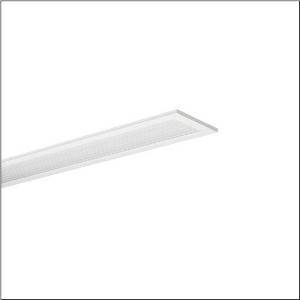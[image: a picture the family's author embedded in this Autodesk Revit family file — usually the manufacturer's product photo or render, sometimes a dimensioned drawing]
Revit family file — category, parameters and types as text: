
# Revit family: apollon_21_linear_51mq15wm2414
name_source: partatom
category: Lighting Fixtures
units: mm (PartAtom-declared; Revit-internal decimal feet)

## family parameters
Cut with Voids When Loaded = No
Host = Face
Light Source = No
Part Type = Normal
Room Calculation Point = No
Round Connector Dimension = Use Diameter
Shared = No

## types (1)
- --- (1 x LED, 4290 lm, 29.7 W, 4000K)
    Apparent Load = 30 VA
    CIE Flux Codes = 66 89 97 100 100
    Color Rendering = 80
    Color Temperature = 4000K
    Default Elevation = 1800 mm
    Description = Apollon 21 linear, office luminaire, primary optical cover: micro prismatic cover, of PMMA, CAT 2 (L<= 3000cd/m²), light emission: direct distribution, primary light characteristic: symmetric, installation type: lay-in mounting, recessed, LED, rated luminous flux: 2.540lm, luminous efficacy: 147lm/W, light colour: 840, colour temperature: 4000K, control gear: ON/OFF Multilumen, with terminal, 3-pole, mains connection: 220..240V, AC/DC, 0/50..60Hz, rated input power: 17.3W, suitable for self-contained emergency lighting element 59MQE002602A with integrated self-test function according to EN 60598-2-22, housing, of aluminium, coated, traffic white (RAL 9016), module: M625, length: 1.245mm, width: 179mm, height: 55mm, housing upper side, of sheet steel, galvanised, protection rating (complete): IP20, protection rating (lamp compartment, on room side): IP50, insulation class (complete): insulation class II (safety insulation), certification: CE, ENEC, UKCA, impact resistance: IK03, permissible operating ambient temperature: -20..+45°C, standard: EN 60598-2-22, corresponds to IFS (International Featured Standards) requirements for safety and quality in the food industry, packaging unit: 1 piece
    Height = 0 mm  [stored 0 ft]
    Lamp = 1 x LED
    Lamp Light Flux = 4290 lm
    Lamp Power = 29.7 W
    Lamp count = 1
    Length = 1245 mm
    Luminous efficacy = 144 lm/W
    Manufacturer = Siteco
    ModVariant = No
    Model = 51MQ15WM2414
    Mounting Place = Ceiling
    Mounting Type = Recessed
    Number of Poles = 1
    OnlyDefault = Yes
    Power Factor = 1
    Product Name = Apollon 21 linear
    Product group = office luminaire | ceiling recessed
    ProductGroupID = 400
    Protection Class = Protection class II
    Protection Degree = IP 20
    RLX_Detail_Level = 1
    RLX_Emergency_Light_Flux = 0 lm
    RLX_Emergency_Type = 0
    RLX_Emergency_Type_DB = No
    RlxData = <blob elided: 14193 chars, md5=fd5aaa6b>
    Socket = socket
    Standby Power = 0 W
    System Light Flux = 4290 lm
    System Power = 30 W
    Type Comments = factory setting: luminous flux: 100 % | (ON | ON | ON) | 700 mA
    Type Image = l_1291018.jpg
    URL = http://relux.com
    VarID = @adj_075821
    Voltage = 0 V
    Weight = 0.00 kg
    Width = 179 mm

note: [stored X ft] marks values corroborated as IEEE doubles in the binary element streams (Revit-internal decimal feet)

## geometry (parser evidence)
native form markers: Sweep x12
no freeform markers — native parametric forms only
